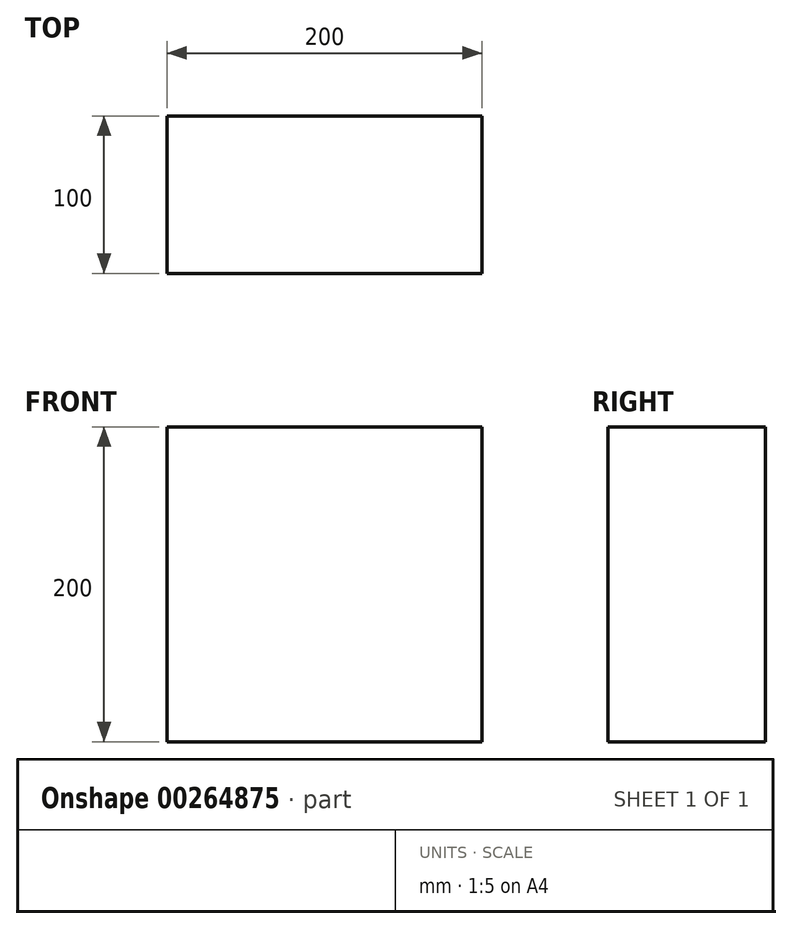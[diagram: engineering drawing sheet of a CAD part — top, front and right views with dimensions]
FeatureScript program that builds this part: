
annotation { "Feature Type Name" : "Feature", "Feature Type Description" : "" }
export const myFeature = defineFeature(function(context is Context, id is Id, definition is map)
    precondition{}
    {
        {
            var Q0;
            Q0=qCreatedBy(makeId("Top.planeOp"),FACE);
            var sketch = newSketch(context, id + "F0", { "sketchPlane" : qUnion([Q0])});
            skLineSegment(sketch, "E0.bottom", {"start": v(-100, 50) * mm, "end": v(100, 50) * mm});
            skLineSegment(sketch, "E0.top", {"start": v(-100, -50) * mm, "end": v(100, -50) * mm});
            skLineSegment(sketch, "E0.left", {"start": v(-100, 50) * mm, "end": v(-100, -50) * mm});
            skLineSegment(sketch, "E0.right", {"start": v(100, 50) * mm, "end": v(100, -50) * mm});
            skLineSegment(sketch, "E1", {"start": v(-100, 50) * mm, "end": v(100, -50) * mm, "construction": true});
            skPoint(sketch, "E2", {"position": v(0, 0) * mm});
            skSolve(sketch);
        }
        {
            var Q0;
            Q0=makeQuery(id+"F0.imprint","IMPRINT",FACE,{"disambiguationData":[TD([[makeQuery(id+"F0.imprint","IMPRINT",EDGE,{"derivedFrom":sQuery(id+"F0.wireOp",EDGE,"E0.bottom")}),-1.0]])]});
            extrude(context, id + "F1", {"entities" : qUnion([Q0]), "depth" : 200 * mm});
        }
    });
